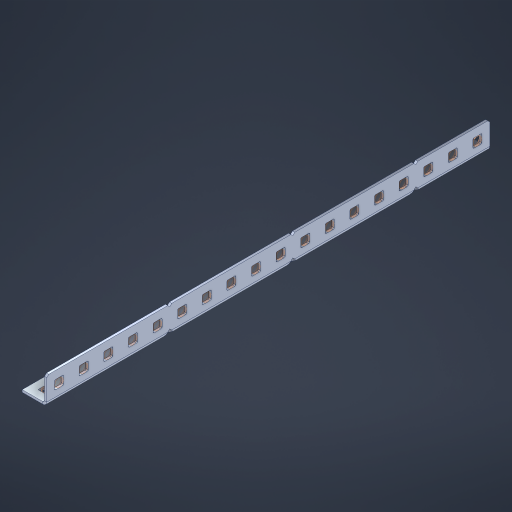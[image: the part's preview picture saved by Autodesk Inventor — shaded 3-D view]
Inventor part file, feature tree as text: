
AUTODESK INVENTOR PART (.ipt)
format: ipt  version: 2023 (Build 270158000, 158)  size: 709,632 bytes
history: native  units: in
note: dims shown in document units (in); Inventor stores cm internally (conversion verified against a paired STEP export)
features: other x41, extrude x35, sheet_metal_op x10, sketch x8, mirror x1, pattern_linear x1, chamfer x1
ambient origin geometry x8: Origin, YZ Plane, XZ Plane, XY Plane, X Axis, Y Axis, Z Axis, Center Point
bodies: Solid1 (feature_tree), Body (feature_tree)
feature tree (97):
  other  "Flange Pattern Plane"
  sheet_metal_op  "Flange Pattern"
  sheet_metal_op  "Body Pattern"
  other  "Arc Length"
  mirror  "Notch Mirror"
  pattern_linear  "Notch Pattern"  Spacing1=0.1875in  [1 undecoded]
  chamfer  "End Chamfer"
  extrude  "Half Cut"  Depth=0.0469in
  sketch  "Sketch1"  dims[d0=2.5in]
  other  "Plate1"
  sketch  "Sketch2"  dims[d1=9.0in]
  other  "Plate2"
  sheet_metal_op  "Bend1"
  sheet_metal_op  "Corner1"
  sketch  "Sketch3"  dims[d2=0.0469in]
  other  "Flange Pattern Sketch"
  sketch  "Sketch7"  dims[d3=0.0469in]
  other  "Srf1"
  other  "Srf2"
  sketch  "Sketch8"  dims[d4=0.0234in]
  sketch  "Sketch9"  dims[d5=0.0938in]
  other  "Srf91"
  sheet_metal_op  "Body Pattern Sketch"
  other  "Srf92"
  sketch  "Sketch13"  dims[d6=0.0469in]
  sketch  "Sketch14"  dims[d7=0.5in d8=90.0deg d9=0.0312in d10=0.1875in d11=0.0469in d12=0.0469in d16=0.182in d17=0.02in d18=0.0469in d19=0.0in d20=0.25in d21=0.25in d46=0.172in d47=1.0in d48=0.0in d49=0.182in d50=0.02in d51=0.25in d52=0.25in d53=0.0469in d54=0.0in d55=0.172in d56=1.0in d57=0.0in d60=7.0866in d62=0.5in d63=0.3937in d65=0.5in d85=0.1227in d86=0.1659in d88=0.04in d89=0.0469in d90=0.0in d91=0.04in d92=0.0491in d95=2.5in d96=0.04in d97=0.25in d98=45.0deg d101=0.0in d102=2.497in d131=0.5in d132=7.0866in d134=0.5in d139=0.5in]
  other  "Srf856"
  other  "Srf1310"
  other  "Srf1311"
  other  "Srf1312"
  other  "Srf1376"
  other  "Srf1377"
  other  "Srf1728"
  other  "Srf1755"
  other  "Srf1878"
  other  "Srf1879"
  other  "Srf1880"
  other  "Srf1881"
  other  "Srf1882"
  other  "Srf1883"
  other  "Srf1884"
  other  "Srf1885"
  other  "Srf1886"
  other  "Srf1887"
  other  "Srf1888"
  other  "Srf1889"
  other  "Srf1942"
  other  "Srf1943"
  other  "Srf1944"
  other  "Srf1945"
  other  "Srf1946"
  other  "Srf1947"
  other  "Srf1948"
  other  "Srf1949"
  other  "Srf1950"
  other  "Srf1951"
  other  "Srf1952"
  other  "Srf1953"
  sheet_metal_op  "Flange Stamp"
  sheet_metal_op  "Flange Circle"
  sheet_metal_op  "Body Stamp"
  sheet_metal_op  "Body Circle"
  sheet_metal_op  "Notch"
  extrude  "ExtrusionSrf2"  Depth=0.0469in
  extrude  "ExtrusionSrf92"  Depth=0.5in
  extrude  "ExtrusionSrf856"  Depth=0.02in
  extrude  "ExtrusionSrf1310"  Depth=0.0469in
  extrude  "ExtrusionSrf1311"  TaperAngle=0.0deg  [1 undecoded]
  extrude  "ExtrusionSrf1312"  Depth=0.5in
  extrude  "ExtrusionSrf1376"  Depth=0.5in
  extrude  "ExtrusionSrf1377"  Depth=0.5in
  extrude  "ExtrusionSrf1728"  Depth=0.5in TaperAngle=0.0deg
  extrude  "ExtrusionSrf1755"  Depth=0.5in
  extrude  "ExtrusionSrf1878"  Depth=0.02in
  extrude  "ExtrusionSrf1879"  Depth=0.5in
  extrude  "ExtrusionSrf1880"  Depth=0.5in
  extrude  "ExtrusionSrf1881"  Depth=0.0469in
  extrude  "ExtrusionSrf1882"  TaperAngle=0.0deg  [1 undecoded]
  extrude  "ExtrusionSrf1883"  Depth=0.5in
  extrude  "ExtrusionSrf1884"  Depth=0.5in TaperAngle=0.0deg
  extrude  "ExtrusionSrf1885"  Depth=0.5in
  extrude  "ExtrusionSrf1886"  Depth=0.5in
  extrude  "ExtrusionSrf1887"  Depth=0.5in
  extrude  "ExtrusionSrf1888"  Depth=0.5in
  extrude  "ExtrusionSrf1889"  Depth=0.5in
  extrude  "ExtrusionSrf1942"  Depth=0.0469in
  extrude  "ExtrusionSrf1943"  TaperAngle=0.0deg  [1 undecoded]
  extrude  "ExtrusionSrf1944"  Depth=0.5in
  extrude  "ExtrusionSrf1945"  Depth=0.5in
  extrude  "ExtrusionSrf1946"  Depth=0.5in
  extrude  "ExtrusionSrf1947"  Depth=0.5in TaperAngle=45.0deg
  extrude  "ExtrusionSrf1948"  TaperAngle=0.0deg  [1 undecoded]
  extrude  "ExtrusionSrf1949"  Depth=0.5in
  extrude  "ExtrusionSrf1950"  Depth=0.5in
  extrude  "ExtrusionSrf1951"  Depth=0.5in
  extrude  "ExtrusionSrf1952"  Depth=0.5in
  extrude  "ExtrusionSrf1953"  Depth=0.5in
note: 5 required parameter values undecoded (feature->parameter linkage not recoverable at this tier; creation-order binding heuristic only, values carry confidence <= 0.55)
